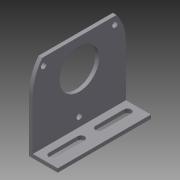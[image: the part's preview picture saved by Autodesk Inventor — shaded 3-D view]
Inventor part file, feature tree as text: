
AUTODESK INVENTOR PART (.ipt)
format: ipt  version: 2015 (Build 190159000, 159)  size: 156,672 bytes
history: native  units: in
note: dims shown in document units (in); Inventor stores cm internally (conversion verified against a paired STEP export)
features: extrude x5, sketch x4, projected_geometry x2
ambient origin geometry x8: Origin, YZ Plane, XZ Plane, XY Plane, X Axis, Y Axis, Z Axis, Center Point
bodies: Solid1 (feature_tree)
feature tree (11):
  extrude  "Extrusion1"  Depth=0.13in
  sketch  "Sketch4"  dims[d2=2.0in d3=3.25in d4=0.0in]
  extrude  "Extrusion3"  Depth=3.25in TaperAngle=0.0deg
  extrude  "Extrusion4"  Depth=1.38in
  extrude  "Extrusion5"  Depth=1.0in TaperAngle=0.0deg
  extrude  "Extrusion6"  Depth=1.0in
  sketch  "Sketch2"  dims[d0=0.13in d1=3.0in]
  projected_geometry  "Projected Loop1"
  sketch  "Sketch5"  dims[d9=1.76in d13=1.38in]
  projected_geometry  "Projected Loop2"
  sketch  "Sketch6"  dims[d14=5.0in d15=0.0in d16=5.0in d17=0.0in d18=1.0in d19=5.0in d20=0.0in d21=0.25in d22=1.0in d23=0.5in d24=5.0in d25=0.0in d26=1.438in d27=0.2in d28=1.1811in d30=360.0deg]
